# Revit family: 63_UN_Downlight_DLM D200_Norton
name_source: partatom
category: Lighting Fixtures
units: mm (PartAtom-declared; Revit-internal decimal feet)

## family parameters
Always vertical = Yes
Cut with Voids When Loaded = No
Light Source = Yes
OmniClass Number = 23.80.70.11.14.11
OmniClass Title = Downlights
Part Type = Normal
Room Calculation Point = Yes
Round Connector Dimension = Use Diameter
Shared = No
Work Plane-Based = No

## types (4) — shared parameters
Apparent Load = 19 VA
Assembly Code = 63.0
Color Filter = 16777215
Dimming Lamp Color Temperature Shift = <None>
Emit Shape Visible in Rendering = No
Emit from Circle Diameter = 120 mm  [stored 0.393701 ft]
Housing_Material = Laminate, White
IK Value = IK07
IP Value = IP44
IfcExportAs = IfcLightFixtureType
IfcExportType = USERDEFINED
Lamp = LED
Manufacturer = Norton
Model = DLM
Tilt Angle = 90.00°
Type Comments = D200
URL = https://www.ivlibrary.com
Voltage = 230 V
Wattage Comments = 19W

## per-type parameters (varying)
| type | Luminous Flux (lm) | Photometric Web File |
| DLMW83LM1200-2300D200 | 2270 lm | DLMW83LM1200-2300D200_LDT.ies |
| DLMW84LM1300-2500D200 | 2450 lm | DLMW84LM1300-2500D200_LDT.ies |
| DLMZ83LM1200-2300D200 | 2270 lm | DLMZ83LM1200-2300D200_LDT.ies |
| DLMZ84LM1300-2500D200 | 2450 lm | DLMZ84LM1300-2500D200_LDT.ies |

note: [stored X ft] marks values corroborated as IEEE doubles in the binary element streams (Revit-internal decimal feet)

## geometry (parser evidence)
native form markers: Sweep x4
no freeform markers — native parametric forms only
